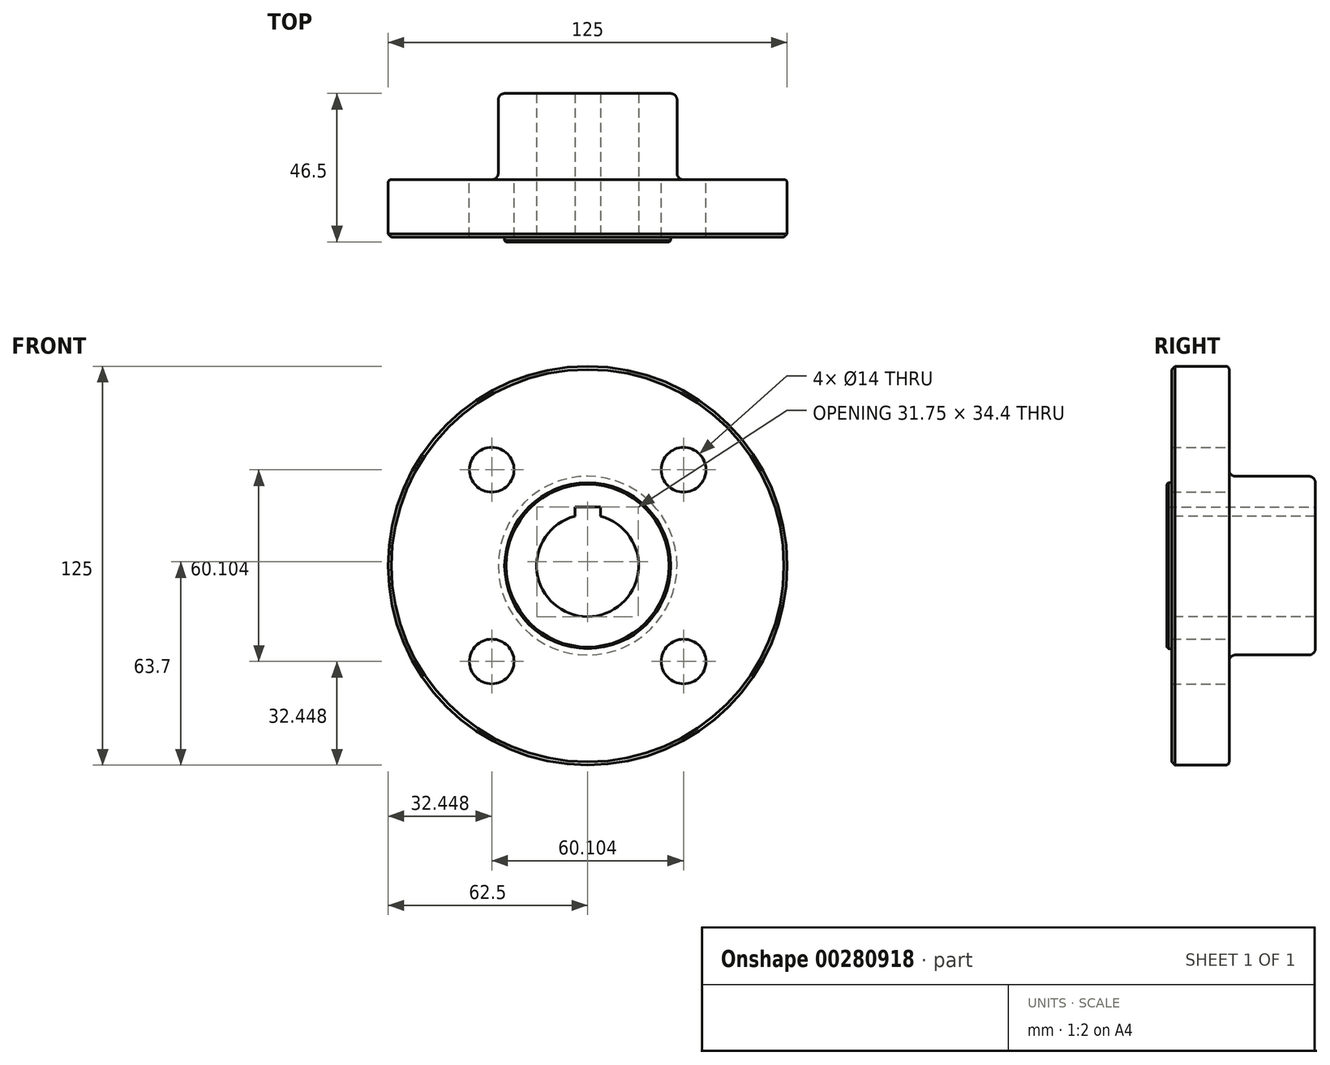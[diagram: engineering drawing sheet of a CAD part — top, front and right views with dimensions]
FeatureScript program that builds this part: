
annotation { "Feature Type Name" : "Feature", "Feature Type Description" : "" }
export const myFeature = defineFeature(function(context is Context, id is Id, definition is map)
    precondition{}
    {
        {
            var Q0;
            Q0=qCreatedBy(makeId("Right.planeOp"),FACE);
            var sketch = newSketch(context, id + "F0", { "sketchPlane" : qUnion([Q0])});
            skLineSegment(sketch, "E0", {"start": v(0, 26) * mm, "end": v(1.5, 26) * mm});
            skLineSegment(sketch, "E1", {"start": v(1.5, 26) * mm, "end": v(1.5, 62.5) * mm});
            skLineSegment(sketch, "E2", {"start": v(1.5, 62.5) * mm, "end": v(19.5, 62.5) * mm});
            skLineSegment(sketch, "E3", {"start": v(19.5, 62.5) * mm, "end": v(19.5, 28) * mm});
            skLineSegment(sketch, "E4", {"start": v(19.5, 28) * mm, "end": v(46.5, 28) * mm});
            skLineSegment(sketch, "E5", {"start": v(46.5, 28) * mm, "end": v(46.5, 16) * mm});
            skLineSegment(sketch, "E6", {"start": v(46.5, 16) * mm, "end": v(0, 16) * mm});
            skLineSegment(sketch, "E7", {"start": v(0, 16) * mm, "end": v(0, 26) * mm});
            skLineSegment(sketch, "E8", {"start": v(-20.7, 0) * mm, "end": v(74.35, 0) * mm, "construction": true});
            skSolve(sketch);
        }
        {
            var Q0;
            Q0=makeQuery(id+"F0.imprint","IMPRINT",FACE,{"disambiguationData":[TD([[makeQuery(id+"F0.imprint","IMPRINT",EDGE,{"derivedFrom":sQuery(id+"F0.wireOp",EDGE,"E0")}),-1.0]])]});
            var Q1;
            Q1=sQuery(id+"F0.wireOp",EDGE,"E8");
            revolve(context, id + "F1", {"entities" : qUnion([Q0]), "axis" : qUnion([Q1]), "revolveType" : RevolveType.FULL});
        }
        {
            var Q0;
            Q0=makeQuery(id+"F1.opRevolve","SWEPT_FACE",FACE,{"disambiguationData":[OSD([sQuery(id+"F0.wireOp",EDGE,"E5")])]});
            var sketch = newSketch(context, id + "F2", { "sketchPlane" : qUnion([Q0])});
            skLineSegment(sketch, "E9.bottom", {"start": v(-4, 18.4) * mm, "end": v(4, 18.4) * mm});
            skLineSegment(sketch, "E9.top", {"start": v(-4, 12) * mm, "end": v(4, 12) * mm});
            skLineSegment(sketch, "E9.left", {"start": v(-4, 18.4) * mm, "end": v(-4, 12) * mm});
            skLineSegment(sketch, "E9.right", {"start": v(4, 18.4) * mm, "end": v(4, 12) * mm});
            skSolve(sketch);
        }
        {
            var Q0;
            {var subQ0=sQuery(id+"F2.wireOp",EDGE,"E9.top");Q0=makeQuery(id+"F2.imprint","IMPRINT",FACE,{"disambiguationData":[TD([[makeQuery(id+"F2.imprint","IMPRINT",EDGE,{"derivedFrom":subQ0}),1.0]])]});}
            var Q1;
            {var subQ0=sQuery(id+"F2.wireOp",EDGE,"E9.bottom");Q1=makeQuery(id+"F2.imprint","IMPRINT",FACE,{"disambiguationData":[TD([[makeQuery(id+"F2.imprint","IMPRINT",EDGE,{"derivedFrom":subQ0}),-1.0]])]});}
            extrude(context, id + "F3", {"entities" : qUnion([Q0, Q1]), "operationType" : NewBodyOperationType.REMOVE, "endBound" : BoundingType.THROUGH_ALL, "oppositeDirection" : true, "depth" : 25 * mm});
        }
        {
            var Q0;
            Q0=makeQuery(id+"F1.opRevolve","SWEPT_FACE",FACE,{"disambiguationData":[OSD([sQuery(id+"F0.wireOp",EDGE,"E3")])]});
            var sketch = newSketch(context, id + "F4", { "sketchPlane" : qUnion([Q0])});
            skLineSegment(sketch, "E10", {"start": v(0, 0) * mm, "end": v(30.05, 30.05) * mm, "construction": true});
            skLineSegment(sketch, "E11.MirrorCS", {"start": v(0, 0) * mm, "end": v(-30.05, 30.05) * mm, "construction": true});
            skLineSegment(sketch, "E12.MirrorCS", {"start": v(0, 0) * mm, "end": v(30.05, -30.05) * mm, "construction": true});
            skLineSegment(sketch, "E13.MirrorCS", {"start": v(0, 0) * mm, "end": v(-30.05, -30.05) * mm, "construction": true});
            skSolve(sketch);
        }
        {
            var Q0;
            Q0=sQuery(id+"F4.wireOp",VERTEX,"E11.MirrorCS.end");
            var Q1;
            Q1=sQuery(id+"F4.wireOp",VERTEX,"E10.end");
            var Q2;
            Q2=sQuery(id+"F4.wireOp",VERTEX,"E13.MirrorCS.end");
            var Q3;
            Q3=sQuery(id+"F4.wireOp",VERTEX,"E12.MirrorCS.end");
            var Q4;
            Q4=makeQuery(id+"F1.opRevolve","SWEPT_BODY",BODY,{"disambiguationData":[OSD([sQuery(id+"F0.wireOp",EDGE,"E0"),sQuery(id+"F0.wireOp",EDGE,"E1"),sQuery(id+"F0.wireOp",EDGE,"E2"),sQuery(id+"F0.wireOp",EDGE,"E3"),sQuery(id+"F0.wireOp",EDGE,"E4"),sQuery(id+"F0.wireOp",EDGE,"E5"),sQuery(id+"F0.wireOp",EDGE,"E6"),sQuery(id+"F0.wireOp",EDGE,"E7")])]});
            hole(context, id + "F5", {"style" : HoleStyle.SIMPLE, "endStyle" : HoleEndStyle.THROUGH, "holeDiameter" : 14 * mm, "tappedDepth" : 12 * mm, "tapClearance" : 3, "locations" : qUnion([Q0, Q1, Q2, Q3]), "scope" : qUnion([Q4])});
        }
        {
            var Q0;
            Q0=makeQuery(id+"F1.opRevolve","SWEPT_EDGE",EDGE,{"disambiguationData":[OSD([sQuery(id+"F0.wireOp",EDGE,"E3"),sQuery(id+"F0.wireOp",EDGE,"E4")])]});
            var Q1;
            Q1=makeQuery(id+"F1.opRevolve","SWEPT_EDGE",EDGE,{"disambiguationData":[OSD([sQuery(id+"F0.wireOp",EDGE,"E4"),sQuery(id+"F0.wireOp",EDGE,"E5")])]});
            fillet(context, id + "F6", {"entities" : qUnion([Q0, Q1]), "radius" : 2 * mm, "tangentPropagation" : true, "allowEdgeOverflow" : false});
        }
        {
            var Q0;
            Q0=makeQuery(id+"F1.opRevolve","SWEPT_EDGE",EDGE,{"disambiguationData":[OSD([sQuery(id+"F0.wireOp",EDGE,"E2"),sQuery(id+"F0.wireOp",EDGE,"E3")])]});
            fillet(context, id + "F7", {"entities" : qUnion([Q0]), "radius" : 1 * mm, "tangentPropagation" : true, "allowEdgeOverflow" : false});
        }
        {
            var Q0;
            Q0=makeQuery(id+"F1.opRevolve","SWEPT_EDGE",EDGE,{"disambiguationData":[OSD([sQuery(id+"F0.wireOp",EDGE,"E1"),sQuery(id+"F0.wireOp",EDGE,"E2")])]});
            chamfer(context, id + "F8", {"entities" : qUnion([Q0]), "width" : 1 * mm, "tangentPropagation" : true});
        }
        {
            var Q0;
            Q0=makeQuery(id+"F1.opRevolve","SWEPT_EDGE",EDGE,{"disambiguationData":[OSD([sQuery(id+"F0.wireOp",EDGE,"E0"),sQuery(id+"F0.wireOp",EDGE,"E7")])]});
            chamfer(context, id + "F9", {"entities" : qUnion([Q0]), "width" : 0.5 * mm, "tangentPropagation" : true});
        }
        {
            var Q0;
            Q0=makeQuery(id+"F1.opRevolve","SWEPT_EDGE",EDGE,{"disambiguationData":[OSD([sQuery(id+"F0.wireOp",EDGE,"E0"),sQuery(id+"F0.wireOp",EDGE,"E1")])]});
            fillet(context, id + "F10", {"entities" : qUnion([Q0]), "radius" : 0.4 * mm, "tangentPropagation" : true, "allowEdgeOverflow" : false});
        }
    });
